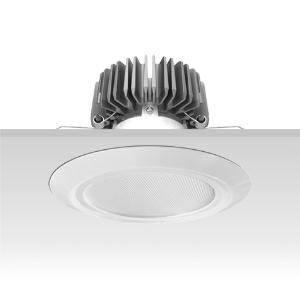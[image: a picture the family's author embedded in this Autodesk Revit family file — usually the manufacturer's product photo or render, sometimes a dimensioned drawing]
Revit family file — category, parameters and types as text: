
# Revit family: 3f_filippi_-_3f_reno_bianco_ampio_3f_filippi_-_30625_a01048_-_3f_reno_200_wh_2000-930_wide___smp_wh_8b7f
name_source: partatom
category: Lighting Fixtures
units: mm (PartAtom-declared; Revit-internal decimal feet)

## family parameters
Cut with Voids When Loaded = No
Host = Face
Light Source = No
Part Type = Normal
Room Calculation Point = No
Round Connector Dimension = Use Diameter
Shared = No

## types (1)
- 3F Filippi - 3F Reno Bianco Ampio (1 x LED, 1650 lm, 24 W, 3000 K)
    Apparent Load = 24 VA
    Approval mark = CE
    CIE Flux Codes = 74 92 98 100 100
    Color Rendering = 90
    Color Temperature = 3000 K
    Control Gear = Electronic ballast
    Default Elevation = 1800 mm
    Description = ILLUMINOTECHNICAL
Luminous efficiency 100% (DLOR 100%, ULOR 0%).
Initial luminous flux of the luminaire 1650 lm.
Direct symmetric wide distribution.
Installation Interdistance Transv.D = 1.06 x hu - Long.D = 1.04 x hu.
Average luminance <3000 cd/m² for radial angles >65°.
Tabular UGR (CIE 117 - 4H-8H; S=0.25H; 70/50/20): RUG 21.3 - 21.1.
Beam angle: 70° - 69°.
Luminous efficacy 69 lm/W.
Lifetime (L90/B10): 30000 h. (tq+25°C)
Lifetime (L85/B10): 50000 h. (tq+25°C)
Lifetime (L70/B10): 80000 h. (tq+25°C)
Sudden decreased luminous flux after 50000 hours: 0% (C0).
Photobiological safety in compliance with IEC/TR 62778: RG0 risk exempt, (IEC 62471).
In compliance with IEC/EN 62722-2-1 - IEC/EN 62717 standards.

SOURCE
Compact LED module 2000/930.
Energy efficiency class (UE 2019/2020 - UE 2019/2015): E.
CIE 13.3 Colour rendering index: CRI >90 (R9 >50%).
IES TM-30 Fidelity Index: Rf = 92 Rg = 101.
CCT nominal colour temperature 3000 K.
Colour initial tolerance (MacAdam): SDCM 3.
Zhaga Book 3 compliant.

MECHANICAL
Passive heat dissipator in die-casting aluminium, oversized, for optimum thermal management of the LED module.
Parabolic element with graduated/concentric rings in white polycarbonate.
Transparent external lens with glossy and satin differentiated surfaces, with a cooling and anti-insect system in methacrylate (PMMA).
Fastening spring clips in stainless steel.
Dimensions: diameter 226 mm, height 146 mm. Weight 1.01 kg.
IP44 protection degree for exposed part, IP20 for recessed part.
Mechanical strength to impacts IK05 (0.7 joule).
Glow-wire test resistance 650°C.

ELECTRICAL
Wiring on a separate unit.
Halogen Free electronic wiring 230V-50/60Hz, power factor 0.95, THD <25%, constant output current, SELV, class II, 1 driver.
Power of the luminaire 24 W.
ENEC - CE.
SAFE FLICKER: PstLM=<1 and SVM=<0.4 (IEC TR 61547-1 and IEC TR 63158), to ensure a more comfortable and safe light.
Luminaire compliant with EN 60598-2-22 for power supply from a centralised emergency system CPSS (Central Power Supply System), not incorporated in the luminaire - high risk areas excluded. The default power and flux are 100% in AC and 100% in DC.
Ambient temperature from 0°C to +25°C.
Temperature class T6 max 85°C.
Relative humidity UR: <85%.

INSTALLATION
Pull-up recessed fitting.
False ceiling carving: 200 mm.
All accessories dedicated to this product are available on the Catalog and on our website www.3F-Filippi.com.

ACCESSORIES
A01048 - Anti-glare microprismatic SMP diffuser in methacrylate (PMMA), locked and in line with the trim, in white polycarbonate.

APPLICATIONS
Suitable product for food production plants (HACCP), IFS (Food Version 6), BRC (GSFS Food Version 7).
Environments: architectural, commercial, exhibition areas, transit areas, corridors, shops, display windows, service areas.
In false ceilings with narrow voids.

WARNING
Luminaire designed for disposal/recycling at end-of-life.
Replaceable (LED only) light source by a professional. Replaceable control gear by a professional.
    Height = 0 mm  [stored 0 ft]
    Lamp = 1 x LED
    Lamp Light Flux = 1650 lm
    Lamp Power = 24 W
    Lamp count = 1
    Length = 226 mm
    Lifetime = 50000 h
    Luminous efficacy = 69 lm/W
    Manufacturer = 3F Filippi
    ModVariant = No
    Model = 3F Filippi - 30625+A01048 - 3F Reno 200 WH 2000-930 WIDE + SMP WH
    Mounting Place = Ceiling
    Mounting Type = Recessed
    Number of Poles = 1
    OnlyDefault = Yes
    Power Factor = 1
    Product Name = 3F Filippi - 3F Reno Bianco Ampio
    Product group = recessed luminaire
    ProductGroupID = 4
    Protection Class = Protection class II
    Protection Degree = IP 20
    RLX_Detail_Level = 1
    RLX_Emergency_Light_Flux = 0 lm
    RLX_Emergency_Type = 0
    RLX_Emergency_Type_DB = No
    RlxData = <blob elided: 95049 chars, md5=a552b3b0>
    Socket = socket
    Standby Power = 0 W
    System Light Flux = 1650 lm
    System Power = 24 W
    Type Comments = Product without accessories
    Type Image = 3ffilippi_3f_reno_200_wh_vs_smp.jpg
    URL = http://relux.com
    VarID = ---
    Voltage = 0 V
    Weight = 0.00 kg
    Width = 0 mm  [stored 0 ft]

note: [stored X ft] marks values corroborated as IEEE doubles in the binary element streams (Revit-internal decimal feet)

## geometry (parser evidence)
native form markers: Blend x4, Sweep x10
no freeform markers — native parametric forms only
